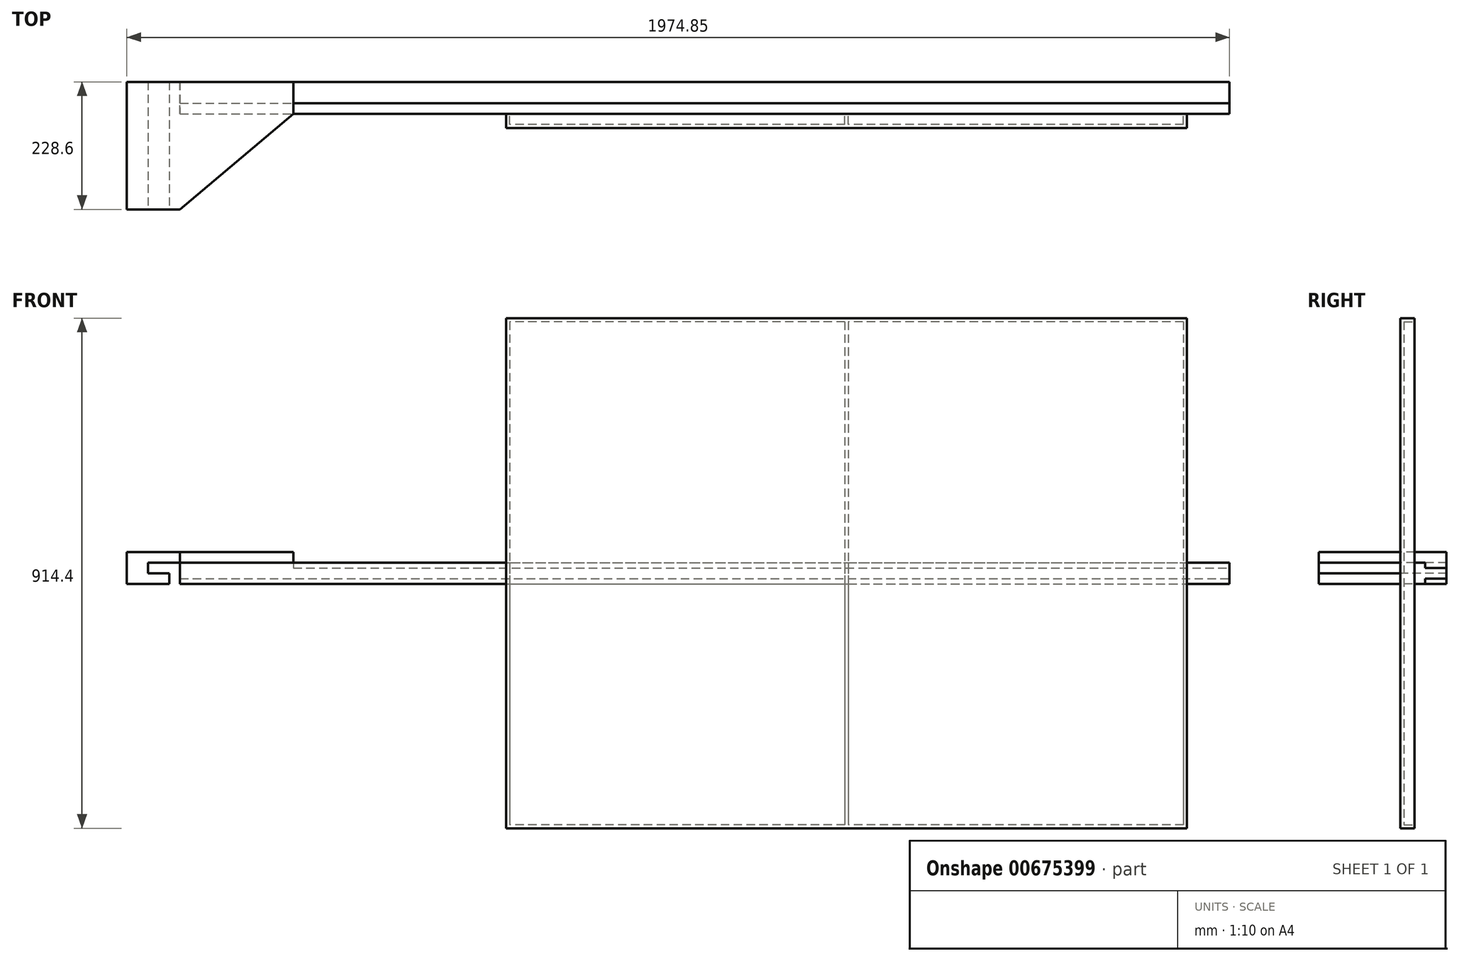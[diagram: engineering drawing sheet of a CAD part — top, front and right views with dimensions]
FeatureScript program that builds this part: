
annotation { "Feature Type Name" : "Feature", "Feature Type Description" : "" }
export const myFeature = defineFeature(function(context is Context, id is Id, definition is map)
    precondition{}
    {
        {
            var Q0;
            Q0=qCreatedBy(makeId("Top.planeOp"),FACE);
            var sketch = newSketch(context, id + "F0", { "sketchPlane" : qUnion([Q0])});
            skLineSegment(sketch, "E0", {"start": v(0, 0) * mm, "end": v(0, 228.6) * mm});
            skLineSegment(sketch, "E1", {"start": v(0, 228.6) * mm, "end": v(298.45, 228.6) * mm});
            skLineSegment(sketch, "E2", {"start": v(298.45, 228.6) * mm, "end": v(298.45, 171.45) * mm});
            skLineSegment(sketch, "E3", {"start": v(298.45, 171.45) * mm, "end": v(95.25, 0) * mm});
            skLineSegment(sketch, "E4", {"start": v(95.25, 0) * mm, "end": v(0, 0) * mm});
            skSolve(sketch);
        }
        {
            var Q0;
            Q0 = qSketchRegion(id + "F0", true);
            extrude(context, id + "F1", {"entities" : qUnion([Q0]), "depth" : 19.05 * mm, "offsetDistance" : 25.4 * mm});
        }
        {
            var Q0;
            Q0=makeQuery(id+"F1.opExtrude","SWEPT_FACE",FACE,{"disambiguationData":[OSD([sQuery(id+"F0.wireOp",EDGE,"E4")])]});
            var sketch = newSketch(context, id + "F2", { "sketchPlane" : qUnion([Q0])});
            skLineSegment(sketch, "E5.bottom", {"start": v(0, 0) * mm, "end": v(38.1, 0) * mm});
            skLineSegment(sketch, "E5.top", {"start": v(0, -38.1) * mm, "end": v(38.1, -38.1) * mm});
            skLineSegment(sketch, "E5.left", {"start": v(0, 0) * mm, "end": v(0, -38.1) * mm});
            skLineSegment(sketch, "E5.right", {"start": v(38.1, 0) * mm, "end": v(38.1, -19.05) * mm});
            skLineSegment(sketch, "E6.bottom", {"start": v(38.1, -38.1) * mm, "end": v(76.2, -38.1) * mm});
            skLineSegment(sketch, "E6.top", {"start": v(38.1, -19.05) * mm, "end": v(76.2, -19.05) * mm});
            skLineSegment(sketch, "E6.right", {"start": v(76.2, -38.1) * mm, "end": v(76.2, -19.05) * mm});
            skSolve(sketch);
        }
        {
            var Q0;
            Q0 = qSketchRegion(id + "F2", true);
            extrude(context, id + "F3", {"entities" : qUnion([Q0]), "operationType" : NewBodyOperationType.ADD, "oppositeDirection" : true, "depth" : 228.6 * mm, "offsetDistance" : 25.4 * mm});
        }
        {
            var Q0;
            Q0=makeQuery(id+"F1.opExtrude","SWEPT_FACE",FACE,{"disambiguationData":[OSD([sQuery(id+"F0.wireOp",EDGE,"E2")])]});
            var sketch = newSketch(context, id + "F4", { "sketchPlane" : qUnion([Q0])});
            skLineSegment(sketch, "E7.bottom", {"start": v(171.45, 0) * mm, "end": v(190.5, 0) * mm});
            skLineSegment(sketch, "E7.top", {"start": v(171.45, -38.1) * mm, "end": v(190.5, -38.1) * mm});
            skLineSegment(sketch, "E7.left", {"start": v(171.45, 0) * mm, "end": v(171.45, -38.1) * mm});
            skLineSegment(sketch, "E7.right", {"start": v(190.5, 0) * mm, "end": v(190.5, -9.53) * mm});
            skLineSegment(sketch, "E8.bottom", {"start": v(190.5, -9.53) * mm, "end": v(228.6, -9.53) * mm});
            skLineSegment(sketch, "E8.top", {"start": v(190.5, -28.58) * mm, "end": v(228.6, -28.58) * mm});
            skLineSegment(sketch, "E8.right", {"start": v(228.6, -9.53) * mm, "end": v(228.6, -28.58) * mm});
            skLineSegment(sketch, "E9.trimOffspring", {"start": v(190.5, -28.58) * mm, "end": v(190.5, -38.1) * mm});
            skSolve(sketch);
        }
        {
            var Q0;
            Q0 = qSketchRegion(id + "F4", true);
            extrude(context, id + "F5", {"entities" : qUnion([Q0]), "operationType" : NewBodyOperationType.ADD, "oppositeDirection" : true, "depth" : 203.2 * mm, "offsetDistance" : 25.4 * mm, "hasSecondDirection" : true, "secondDirectionOppositeDirection" : false, "secondDirectionDepth" : 1676.4 * mm});
        }
        {
            var Q0;
            Q0=makeQuery(id+"F1.opExtrude","SWEPT_FACE",FACE,{"disambiguationData":[OSD([sQuery(id+"F0.wireOp",EDGE,"E2")])]});
            var sketch = newSketch(context, id + "F6", { "sketchPlane" : qUnion([Q0])});
            skLineSegment(sketch, "E10.bottom", {"start": v(190.5, 0) * mm, "end": v(228.6, 0) * mm});
            skLineSegment(sketch, "E10.top", {"start": v(190.5, -9.53) * mm, "end": v(228.6, -9.53) * mm});
            skLineSegment(sketch, "E10.left", {"start": v(190.5, 0) * mm, "end": v(190.5, -9.53) * mm});
            skLineSegment(sketch, "E10.right", {"start": v(228.6, 0) * mm, "end": v(228.6, -9.53) * mm});
            skSolve(sketch);
        }
        {
            var Q0;
            Q0 = qSketchRegion(id + "F6", true);
            extrude(context, id + "F7", {"entities" : qUnion([Q0]), "operationType" : NewBodyOperationType.ADD, "oppositeDirection" : true, "depth" : 203.2 * mm, "offsetDistance" : 25.4 * mm});
        }
        {
            var Q0;
            Q0=makeQuery(id+"F5.opExtrude","SWEPT_FACE",FACE,{"disambiguationData":[OSD([sQuery(id+"F4.wireOp",EDGE,"E7.left")])]});
            var sketch = newSketch(context, id + "F8", { "sketchPlane" : qUnion([Q0])});
            skLineSegment(sketch, "E11.bottom", {"start": v(679.45, 438.15) * mm, "end": v(1898.65, 438.15) * mm});
            skLineSegment(sketch, "E11.top", {"start": v(679.45, -476.25) * mm, "end": v(1898.65, -476.25) * mm});
            skLineSegment(sketch, "E11.left", {"start": v(679.45, 438.15) * mm, "end": v(679.45, -476.25) * mm});
            skLineSegment(sketch, "E11.right", {"start": v(1898.65, 438.15) * mm, "end": v(1898.65, -476.25) * mm});
            skSolve(sketch);
        }
        {
            var Q0;
            Q0 = qSketchRegion(id + "F8", true);
            extrude(context, id + "F9", {"entities" : qUnion([Q0]), "operationType" : NewBodyOperationType.ADD, "depth" : 25.4 * mm, "offsetDistance" : 25.4 * mm});
        }
        {
            var Q0;
            {var subQ0=sQuery(id+"F8.wireOp",EDGE,"E11.left");var subQ1=sQuery(id+"F8.wireOp",EDGE,"E11.top");var subQ2=sQuery(id+"F8.wireOp",EDGE,"E11.right");Q0=makeQuery(id+"F9.boolean.opBoolean","SPLIT",FACE,{"disambiguationData":[TD([makeQuery(id+"F5.opExtrude","SWEPT_FACE",FACE,{"disambiguationData":[OSD([sQuery(id+"F4.wireOp",EDGE,"E7.top")])]})])],"derivedFrom":makeQuery(id+"F9.opExtrude","CAP_FACE",FACE,{"disambiguationData":[OSD([sQuery(id+"F8.wireOp",EDGE,"E11.bottom"),subQ1,subQ0,subQ2])],"isStart":true})});}
            var sketch = newSketch(context, id + "F10", { "sketchPlane" : qUnion([Q0])});
            skLineSegment(sketch, "E12.bottom", {"start": v(-1892.3, 431.8) * mm, "end": v(-1292.23, 431.8) * mm});
            skLineSegment(sketch, "E12.top", {"start": v(-1892.3, -469.9) * mm, "end": v(-1292.23, -469.9) * mm});
            skLineSegment(sketch, "E12.left", {"start": v(-1892.3, 431.8) * mm, "end": v(-1892.3, -469.9) * mm});
            skLineSegment(sketch, "E12.right", {"start": v(-1292.23, 431.8) * mm, "end": v(-1292.23, -469.9) * mm});
            skLineSegment(sketch, "E13.bottom", {"start": v(-1285.88, 431.8) * mm, "end": v(-685.8, 431.8) * mm});
            skLineSegment(sketch, "E13.top", {"start": v(-1285.88, -469.9) * mm, "end": v(-685.8, -469.9) * mm});
            skLineSegment(sketch, "E13.left", {"start": v(-1285.88, 431.8) * mm, "end": v(-1285.88, -469.9) * mm});
            skLineSegment(sketch, "E13.right", {"start": v(-685.8, 431.8) * mm, "end": v(-685.8, -469.9) * mm});
            skSolve(sketch);
        }
        {
            var Q0;
            Q0 = qSketchRegion(id + "F10", true);
            extrude(context, id + "F11", {"entities" : qUnion([Q0]), "operationType" : NewBodyOperationType.REMOVE, "oppositeDirection" : true, "depth" : 19.05 * mm, "offsetDistance" : 25.4 * mm});
        }
    });
